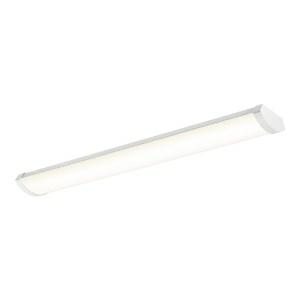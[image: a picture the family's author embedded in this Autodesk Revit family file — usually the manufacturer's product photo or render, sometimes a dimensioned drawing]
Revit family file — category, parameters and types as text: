
# Revit family: ledlinear-e_cl15-53w-4000-wh_542005040000
name_source: partatom
category: Leuchten
revit_build: Autodesk Revit 2016 (Build: 20190508_0715(x64)
units: mm (PartAtom-declared; Revit-internal decimal feet)

## family parameters
Basisbauteil = Fläche
Beim Laden mit Abzugskörper schneiden = Nein
Bemaßung runder Anschluss = Durchmesser verwenden
Gemeinsam genutzt = Nein
Lichtquelle = Nein
Raumberechnungspunkt = Nein
Teiletyp = Normal

## types (1)
- LEDLinear-E CL15-53W-4000-WH (1 x LED, 6360 lm)
    Approval mark = CE
    Beschreibung = Easy to install LED linear solution. Elegant but sturdy design: IP44 and IK06. Comfortable light due to opal diffusor. Central or side power connection. Motion and daylight sensor accessory available.
    CIE Flux Codes = 44 74 91 95 100
    Control Gear = Electronic ballast
    Height = 75 mm
    Hersteller = OPPLE
    Lamp Light Flux = 6360 lm
    Lamp count = 1
    Lampe = 1 x LED
    Length = 180 mm  [stored 0.590551 ft]
    Luminous efficacy = 120 lm/W
    ModVariant = Nein
    Modell = 542005040000
    Mounting Place = Ceiling
    Mounting Type = Surface mounted
    Number of Poles = 1
    OnlyDefault = Ja
    Power Factor = 1
    Product Name = LEDLinear-E CL15-53W-4000-WH
    Product group = Linear EcoMax
    ProductGroupID = 303
    Protection Class = Protection class I
    Protection Degree = IP 44
    RLX_Detail_Level = 1
    RlxData = <blob elided: 95585 chars, md5=9f1f58e2>
    Scheinlast = 53 VA
    Socket = socket
    Standby Power = 0 W
    System Light Flux = 6360 lm
    System Power = 53 W
    Typenbild = 542005040000.jpg
    Typenkommentare = Product without accessories
    URL = http://relux.com
    VarID = ---
    Voltage = 0 V
    Vorgabe-Ansicht = 1800 mm
    Weight = 0.00 kg
    Width = 1500 mm

note: [stored X ft] marks values corroborated as IEEE doubles in the binary element streams (Revit-internal decimal feet)

## geometry (parser evidence)
native form markers: Blend x4, Sweep x15
no freeform markers — native parametric forms only
